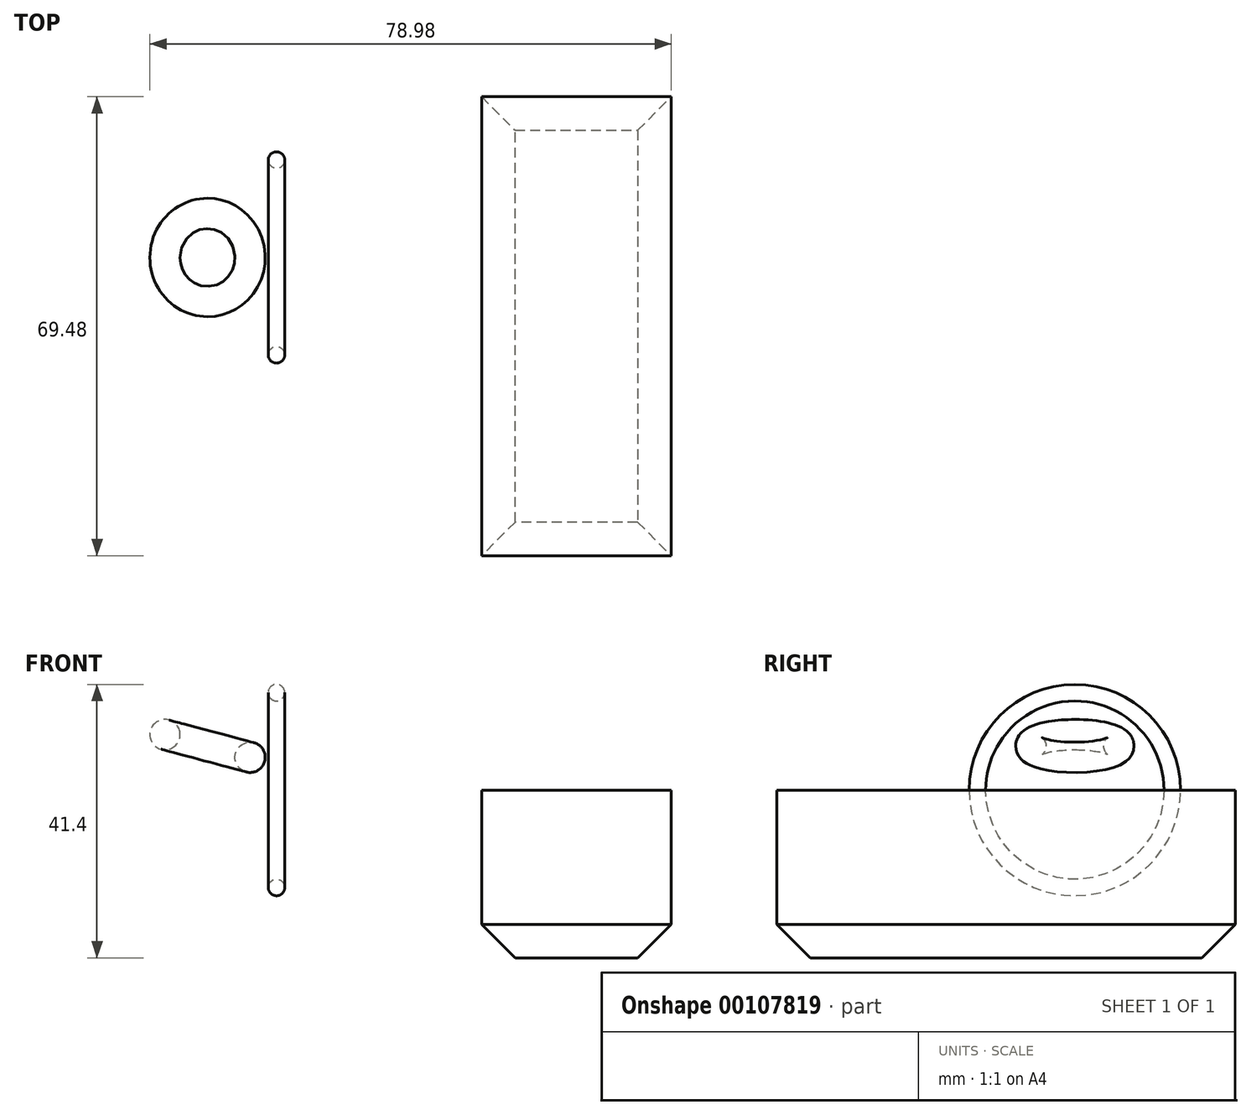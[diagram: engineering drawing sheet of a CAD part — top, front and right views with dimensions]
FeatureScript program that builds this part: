
annotation { "Feature Type Name" : "Feature", "Feature Type Description" : "" }
export const myFeature = defineFeature(function(context is Context, id is Id, definition is map)
    precondition{}
    {
        {
            var Q0;
            Q0=qCreatedBy(makeId("Front.planeOp"),FACE);
            var sketch = newSketch(context, id + "F0", { "sketchPlane" : qUnion([Q0])});
            skLineSegment(sketch, "E0", {"start": v(0, 0) * mm, "end": v(7.1, 0) * mm, "construction": true});
            skCircle(sketch, "E1", {"center": v(0, 14.75) * mm, "radius": 1.25 * mm});
            skPoint(sketch, "E2", {"position": v(0, 13.5) * mm});
            skSolve(sketch);
        }
        {
            var Q0;
            Q0=makeQuery(id+"F0.imprint","IMPRINT",FACE,{"disambiguationData":[TD([[makeQuery(id+"F0.imprint","IMPRINT",EDGE,{"derivedFrom":sQuery(id+"F0.wireOp",EDGE,"E1")}),1.0]])]});
            var Q1;
            Q1=sQuery(id+"F0.wireOp",EDGE,"E0");
            revolve(context, id + "F1", {"entities" : qUnion([Q0]), "axis" : qUnion([Q1]), "revolveType" : RevolveType.FULL});
        }
        {
            var Q0;
            Q0 = qSketchRegion(id + "F0", true);
            var sketch = newSketch(context, id + "F4", { "sketchPlane" : qUnion([Q0])});
            skCircle(sketch, "E3", {"center": v(-16.9, 8.4) * mm, "radius": 2.3 * mm});
            skLineSegment(sketch, "E4", {"start": v(-20.27, -30.16) * mm, "end": v(-15.1, -10.74) * mm});
            skSolve(sketch);
        }
        {
            var Q0;
            Q0=makeQuery(id+"F4.imprint","IMPRINT",FACE,{"disambiguationData":[TD([[makeQuery(id+"F4.imprint","IMPRINT",EDGE,{"derivedFrom":sQuery(id+"F4.wireOp",EDGE,"E3")}),1.0]])]});
            var Q1;
            Q1=sQuery(id+"F4.wireOp",EDGE,"E4");
            revolve(context, id + "F5", {"entities" : qUnion([Q0]), "axis" : qUnion([Q1]), "revolveType" : RevolveType.FULL});
        }
        {
            var Q0;
            Q0=qCreatedBy(makeId("Top.planeOp"),FACE);
            var sketch = newSketch(context, id + "F6", { "sketchPlane" : qUnion([Q0])});
            skLineSegment(sketch, "E5.bottom", {"start": v(31.07, 24.33) * mm, "end": v(59.8, 24.33) * mm});
            skLineSegment(sketch, "E5.top", {"start": v(31.07, -45.15) * mm, "end": v(59.8, -45.15) * mm});
            skLineSegment(sketch, "E5.left", {"start": v(31.07, 24.33) * mm, "end": v(31.07, -45.15) * mm});
            skLineSegment(sketch, "E5.right", {"start": v(59.8, 24.33) * mm, "end": v(59.8, -45.15) * mm});
            skSolve(sketch);
        }
        {
            var Q0;
            Q0 = qSketchRegion(id + "F6", true);
            extrude(context, id + "F7", {"entities" : qUnion([Q0]), "oppositeDirection" : true, "depth" : 25.4 * mm});
        }
        {
            var Q0;
            Q0=makeQuery(id+"F7.opExtrude","CAP_EDGE",EDGE,{"disambiguationData":[OSD([sQuery(id+"F6.wireOp",EDGE,"E5.right")])],"isStart":false});
            var Q1;
            Q1=makeQuery(id+"F7.opExtrude","CAP_EDGE",EDGE,{"disambiguationData":[OSD([sQuery(id+"F6.wireOp",EDGE,"E5.top")])],"isStart":false});
            var Q2;
            Q2=makeQuery(id+"F7.opExtrude","CAP_EDGE",EDGE,{"disambiguationData":[OSD([sQuery(id+"F6.wireOp",EDGE,"E5.bottom")])],"isStart":false});
            var Q3;
            Q3=makeQuery(id+"F7.opExtrude","CAP_EDGE",EDGE,{"disambiguationData":[OSD([sQuery(id+"F6.wireOp",EDGE,"E5.left")])],"isStart":false});
            chamfer(context, id + "F2", {"entities" : qUnion([Q0, Q1, Q2, Q3]), "width" : 5.08 * mm, "tangentPropagation" : true});
        }
    });
